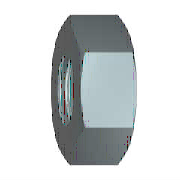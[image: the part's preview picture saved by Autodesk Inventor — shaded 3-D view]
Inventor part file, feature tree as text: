
AUTODESK INVENTOR PART (.ipt)
format: ipt  version: 2025.1 (Build 291241020, 241B)  size: 162,816 bytes
history: native  units: mm (DEFAULTED — no unit token found)
features: chamfer x1, hole x1, other x1, plane x1
ambient origin geometry x7: Origin, YZ Plane, XZ Plane, X Axis, Y Axis, Z Axis, Center Point
bodies: Solid1 (feature_tree), Body (feature_tree)
feature tree (4):
  chamfer  "Chamfer1"  Distance=63.50853mm
  hole  "Thread"  [1 undecoded]
  other  "Work Axis1"
  plane  "Work Plane1"
note: 1 required parameter value undecoded (feature->parameter linkage not recoverable at this tier; creation-order binding heuristic only, values carry confidence <= 0.55)
